# Revit family: QF_ELECTROLUXPROFESSIONAL_237305_ECOE201K2GB
name_source: partatom
category: Attrezzature speciali
units: mm (PartAtom-declared; Revit-internal decimal feet)

## family parameters
Attiva taglio nelle viste = No
Basato su piano di lavoro = No
Condiviso = No
Mantieni orientamento annotazione = No
Punto di calcolo locali = No
Quota connettore circolare = Usa diametro
Sempre verticale = Sì
Taglio con vuoti quando caricato = No
Tipo di parte = Normale

## types (1)
- QF_ELECTROLUXPROFESSIONAL_237305_ECOE201K2GB
    Accessory = Sì
    Cold Water Size = 19 mm
    Compressed Air Pressure = 0.0 Pa
    Compressed Air Size = 0 mm
    Compressed Air Volume = 0.0 L/s
    Condensate Return Size = 0 mm
    Cycle = 50 Hz
    Depth Actual = 939 mm  [stored 3.08071 ft]
    Descrizione = SKYLINE PROS OVEN 16 400x600MM - GAS - BAKERY
    Direct Waste Size = 50 mm
    Gas Input Pressure = 0
    Gas KW = 54
    Gas Size = 25 mm
    HP = 2.4 HP
    Height Actual = 1794 mm  [stored 5.88583 ft]
    Hot Water Size = 0 mm
    Item Number = 237534
    Length Actual = 911 mm  [stored 2.98885 ft]
    Modello = ECOE201K2GB
    Phase = 1
    Produttore = Electrolux
    Prospetto di default = 0 mm  [stored 0 ft]
    Refrigerant Compressor Remote = Sì
    Refrigeration Liquid Line Size = 0 mm
    Refrigeration Suction Line Size = 0 mm
    Steam Pounds per Hour = 0
    Steam Supply Maximum Pressure = 0.0 Pa
    Steam Supply Minimum Pressure = 0.0 Pa
    Steam Supply Size = 0 mm
    URL = http://professional.electrolux.com
    URL Manufacturer = http://professional.electrolux.com
    Volts = 220 V
    Watts = 0 W
    Weight = 0.00 kg

note: source unit labels omitted for Gas Input Pressure — the stored unit's dimension contradicts the parameter name (converter mislabeling)

note: [stored X ft] marks values corroborated as IEEE doubles in the binary element streams (Revit-internal decimal feet)
